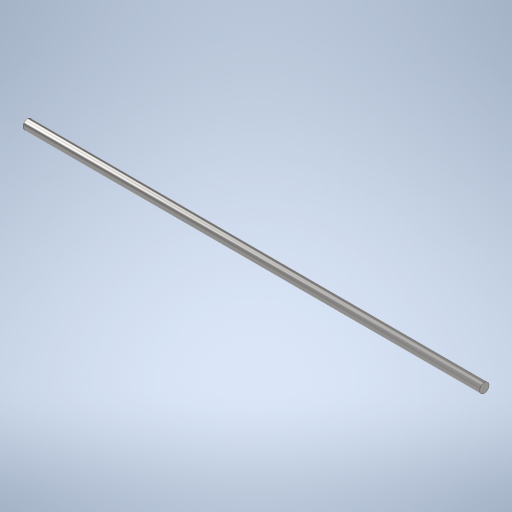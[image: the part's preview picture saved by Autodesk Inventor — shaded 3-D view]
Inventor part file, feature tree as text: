
AUTODESK INVENTOR PART (.ipt)
format: ipt  version: 2024 (Build 280153000, 153)  size: 265,216 bytes
history: native  units: in
note: dims shown in document units (in); Inventor stores cm internally (conversion verified against a paired STEP export)
features: extrude x3, sketch x3, projected_geometry x1
ambient origin geometry x8: Origin, YZ Plane, XZ Plane, XY Plane, X Axis, Y Axis, Z Axis, Center Point
bodies: Solid1 (feature_tree)
feature tree (7):
  extrude  "Extrusion1"  Depth=12.0in TaperAngle=0.0deg
  extrude  "Extrusion2"  Depth=15.1688in TaperAngle=0.0deg
  extrude  "Extrusion3"  Depth=32.2313in TaperAngle=0.0deg
  sketch  "Sketch1"  dims[d0=0.5in d1=12.0in d2=0.0in]
  sketch  "Sketch2"  dims[d3=0.375in d4=15.1688in d5=0.0in]
  sketch  "Sketch3"  dims[d6=0.25in d7=32.2313in d8=0.0in]
  projected_geometry  "Projected Loop1"
